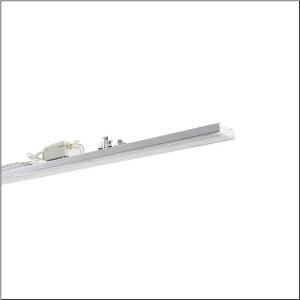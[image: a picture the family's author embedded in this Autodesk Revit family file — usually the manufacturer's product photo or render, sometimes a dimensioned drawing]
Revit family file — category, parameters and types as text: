
# Revit family: licross_r__21_recessed_ho_52te12dv4l2md_2c6d
name_source: partatom
category: Lighting Fixtures
units: mm (PartAtom-declared; Revit-internal decimal feet)

## family parameters
Cut with Voids When Loaded = No
Host = Face
Light Source = No
Part Type = Normal
Room Calculation Point = No
Round Connector Dimension = Use Diameter
Shared = No

## types (1)
- --- (1 x LED, 22710 lm, 125.6 W, 4000K)
    Apparent Load = 126 VA
    CIE Flux Codes = 69 91 98 100 100
    Color Rendering = 80
    Color Temperature = 4000K
    Default Elevation = 1800 mm
    Description = Licross® 21 Recessed HO, luminaire insert, of sheet steel, galvanised, coil coated, white, length: 2.250mm, width: 66mm, height: 67mm, LED rated luminous flux: 22.710lm, light colour: 840, control gear: DALI 2, with plug, 6-pole, with phase selection, mains connection: 220..240V, AC/DC, 0/50..60Hz, rated input power: 126W, without changeover relay, for emergency light function, for central battery installations according to DIN EN 60598-2-22, halogen-free wiring, primary optical cover: cover, of PMMA, light emission: direct distribution, primary light characteristic: symmetric, protection rating (complete): IP54, insulation class (complete): insulation class I (protective earthing), certification: CE, ENEC, VDE, UKCA, protection symbol: D if used in an environment with non-conductive dust loads with corresponding accessories, impact resistance: IK06, permissible ambient temperature for indoor applications: -40..+30°C, standard: EN 60598-2-22, corresponds to IFS (International Featured Standards) requirements for safety and quality in the food industry, reducing of maximum allowable ambient temperature of 5°C with ceiling mounting, LABS conformity tested according to VDMA 24364:2018-05, packaging unit: 1 piece
    Height = 58 mm
    Lamp = 1 x LED
    Lamp Light Flux = 22710 lm
    Lamp Power = 125.6 W
    Lamp count = 1
    Length = 2250 mm
    Luminous efficacy = 181 lm/W
    Manufacturer = Siteco
    ModVariant = No
    Model = 52TE12DV4L2MD
    Mounting Place = Ceiling
    Mounting Type = Pendant
    Number of Poles = 1
    OnlyDefault = Yes
    Power Factor = 1
    Product Name = Licross® 21 Recessed HO
    Product group = luminaire insert
    ProductGroupID = 901
    Protection Class = Protection class I
    Protection Degree = IP 54
    RLX_Detail_Level = 1
    RLX_Emergency_Light_Flux = 0 lm
    RLX_Emergency_Type = 0
    RLX_Emergency_Type_DB = No
    RlxData = <blob elided: 30149 chars, md5=9eb5a782>
    Socket = socket
    Standby Power = 0 W
    System Light Flux = 22710 lm
    System Power = 126 W
    Type Comments = : AC-mode, luminous flux: 100 % | dim-lin: 254 | 489 mA
    Type Image = l_1296930.jpg
    URL = http://relux.com
    VarID = @adj_041765
    Voltage = 0 V
    Weight = 0.00 kg
    Width = 66 mm

## geometry (parser evidence)
native form markers: Blend x4, Sweep x10
no freeform markers — native parametric forms only
